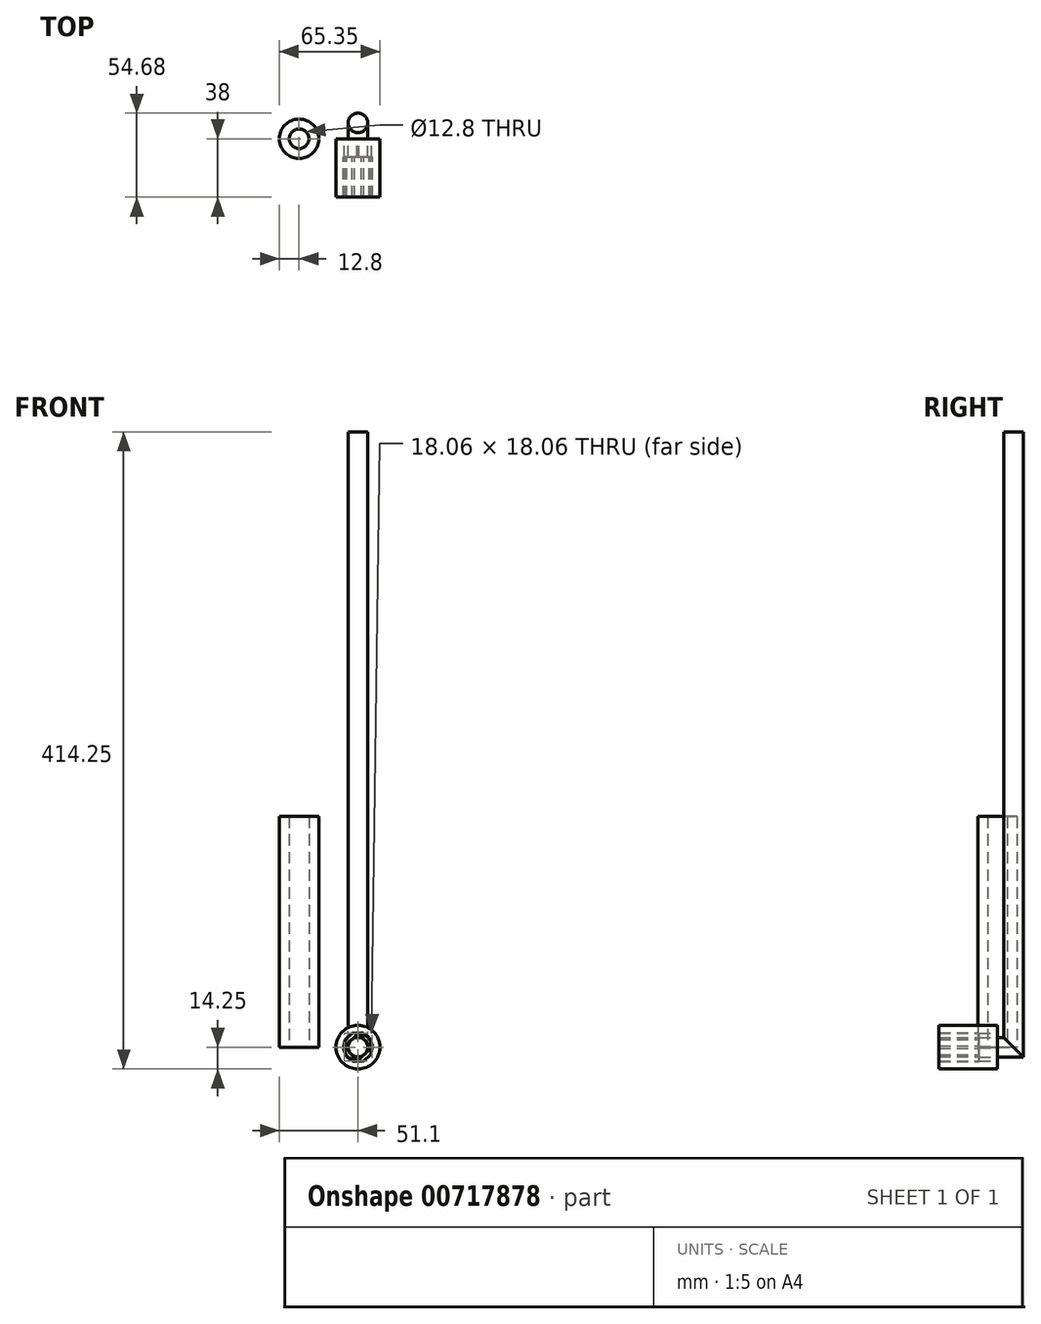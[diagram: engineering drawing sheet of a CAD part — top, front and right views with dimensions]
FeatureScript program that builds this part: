
annotation { "Feature Type Name" : "Feature", "Feature Type Description" : "" }
export const myFeature = defineFeature(function(context is Context, id is Id, definition is map)
    precondition{}
    {
        {
            var Q0;
            Q0=qCreatedBy(makeId("Front.planeOp"),FACE);
            var sketch = newSketch(context, id + "F0", { "sketchPlane" : qUnion([Q0])});
            skCircle(sketch, "E0", {"center": v(0, 0) * mm, "radius": 14.25 * mm});
            skSolve(sketch);
        }
        {
            var Q0;
            Q0 = qSketchRegion(id + "F0", true);
            extrude(context, id + "F1", {"entities" : qUnion([Q0]), "depth" : 38 * mm, "offsetDistance" : 25 * mm});
        }
        {
            var Q0;
            Q0=qCreatedBy(makeId("Front.planeOp"),FACE);
            var sketch = newSketch(context, id + "F2", { "sketchPlane" : qUnion([Q0])});
            skLineSegment(sketch, "E1.0", {"start": v(8.27, -5.03) * mm, "end": v(3.73, -8.92) * mm});
            skLineSegment(sketch, "E1.1", {"start": v(3.73, -8.92) * mm, "end": v(-2.23, -9.41) * mm});
            skLineSegment(sketch, "E1.2", {"start": v(-2.23, -9.41) * mm, "end": v(-7.33, -6.3) * mm});
            skLineSegment(sketch, "E1.3", {"start": v(-7.33, -6.3) * mm, "end": v(-9.64, -0.8) * mm});
            skLineSegment(sketch, "E1.4", {"start": v(-9.64, -0.8) * mm, "end": v(-8.27, 5.03) * mm});
            skLineSegment(sketch, "E1.5", {"start": v(-8.27, 5.03) * mm, "end": v(-3.73, 8.92) * mm});
            skLineSegment(sketch, "E1.6", {"start": v(-3.73, 8.92) * mm, "end": v(2.23, 9.41) * mm});
            skLineSegment(sketch, "E1.7", {"start": v(2.23, 9.41) * mm, "end": v(7.33, 6.3) * mm});
            skLineSegment(sketch, "E1.8", {"start": v(7.33, 6.3) * mm, "end": v(9.64, 0.8) * mm});
            skLineSegment(sketch, "E1.9", {"start": v(9.64, 0.8) * mm, "end": v(8.27, -5.03) * mm});
            skPoint(sketch, "E1.0.midPoint", {"position": v(6, -6.98) * mm});
            skSolve(sketch);
        }
        {
            var Q0;
            Q0 = qSketchRegion(id + "F2", true);
            extrude(context, id + "F3", {"entities" : qUnion([Q0]), "operationType" : NewBodyOperationType.REMOVE, "depth" : 40 * mm, "offsetDistance" : 25 * mm});
        }
        {
            var Q0;
            Q0 = qSketchRegion(id + "F2", true);
            extrude(context, id + "F4", {"entities" : qUnion([Q0]), "operationType" : NewBodyOperationType.ADD, "depth" : 12 * mm, "offsetDistance" : 25 * mm});
        }
        {
            var Q0;
            Q0=qCreatedBy(makeId("Front.planeOp"),FACE);
            var sketch = newSketch(context, id + "F5", { "sketchPlane" : qUnion([Q0])});
            skCircle(sketch, "E2.cCircle", {"center": v(0, 0) * mm, "radius": 6.4 * mm, "construction": true});
            skLineSegment(sketch, "E2.0", {"start": v(9.03, -0.59) * mm, "end": v(-0.59, -9.03) * mm});
            skLineSegment(sketch, "E2.1", {"start": v(-0.59, -9.03) * mm, "end": v(-9.03, 0.59) * mm});
            skLineSegment(sketch, "E2.2", {"start": v(-9.03, 0.59) * mm, "end": v(0.59, 9.03) * mm});
            skLineSegment(sketch, "E2.3", {"start": v(0.59, 9.03) * mm, "end": v(9.03, -0.59) * mm});
            skPoint(sketch, "E2.0.midPoint", {"position": v(4.22, -4.81) * mm});
            skSolve(sketch);
        }
        {
            var Q0;
            Q0 = qSketchRegion(id + "F5", true);
            extrude(context, id + "F6", {"entities" : qUnion([Q0]), "operationType" : NewBodyOperationType.REMOVE, "depth" : 15 * mm, "offsetDistance" : 25 * mm});
        }
        {
            var Q0;
            Q0=qCreatedBy(makeId("Front.planeOp"),FACE);
            var sketch = newSketch(context, id + "F7", { "sketchPlane" : qUnion([Q0])});
            skCircle(sketch, "E3", {"center": v(0, 0) * mm, "radius": 6.35 * mm});
            skSolve(sketch);
        }
        {
            var Q0;
            Q0=qCreatedBy(makeId("Right.planeOp"),FACE);
            var sketch = newSketch(context, id + "F8", { "sketchPlane" : qUnion([Q0])});
            skLineSegment(sketch, "E4", {"start": v(0, 0) * mm, "end": v(10.32, 0) * mm});
            skLineSegment(sketch, "E5", {"start": v(10.32, 0) * mm, "end": v(10.32, 400) * mm});
            skLineSegment(sketch, "E6", {"start": v(0, 0) * mm, "end": v(-12, 0) * mm});
            skSolve(sketch);
        }
        {
            var Q0;
            Q0 = qSketchRegion(id + "F7", true);
            var Q1;
            Q1=sQuery(id+"F8.wireOp",EDGE,"E5");
            var Q2;
            Q2=sQuery(id+"F8.wireOp",EDGE,"E4");
            sweep(context, id + "F9", {"profiles" : qUnion([Q0]), "path" : qUnion([Q1, Q2])});
        }
        {
            var Q0;
            Q0=qCreatedBy(makeId("Top.planeOp"),FACE);
            var sketch = newSketch(context, id + "F10", { "sketchPlane" : qUnion([Q0])});
            skCircle(sketch, "E7", {"center": v(-38.3, 0) * mm, "radius": 12.8 * mm});
            skCircle(sketch, "E8", {"center": v(-38.3, 0) * mm, "radius": 6.4 * mm});
            skSolve(sketch);
        }
        {
            var Q0;
            Q0 = qSketchRegion(id + "F10", true);
            extrude(context, id + "F11", {"entities" : qUnion([Q0]), "depth" : 150 * mm, "offsetDistance" : 25 * mm});
        }
        {
            var Q0;
            Q0 = qSketchRegion(id + "F7", true);
            extrude(context, id + "F12", {"entities" : qUnion([Q0]), "operationType" : NewBodyOperationType.ADD, "depth" : 12 * mm, "offsetDistance" : 25 * mm});
        }
    });
